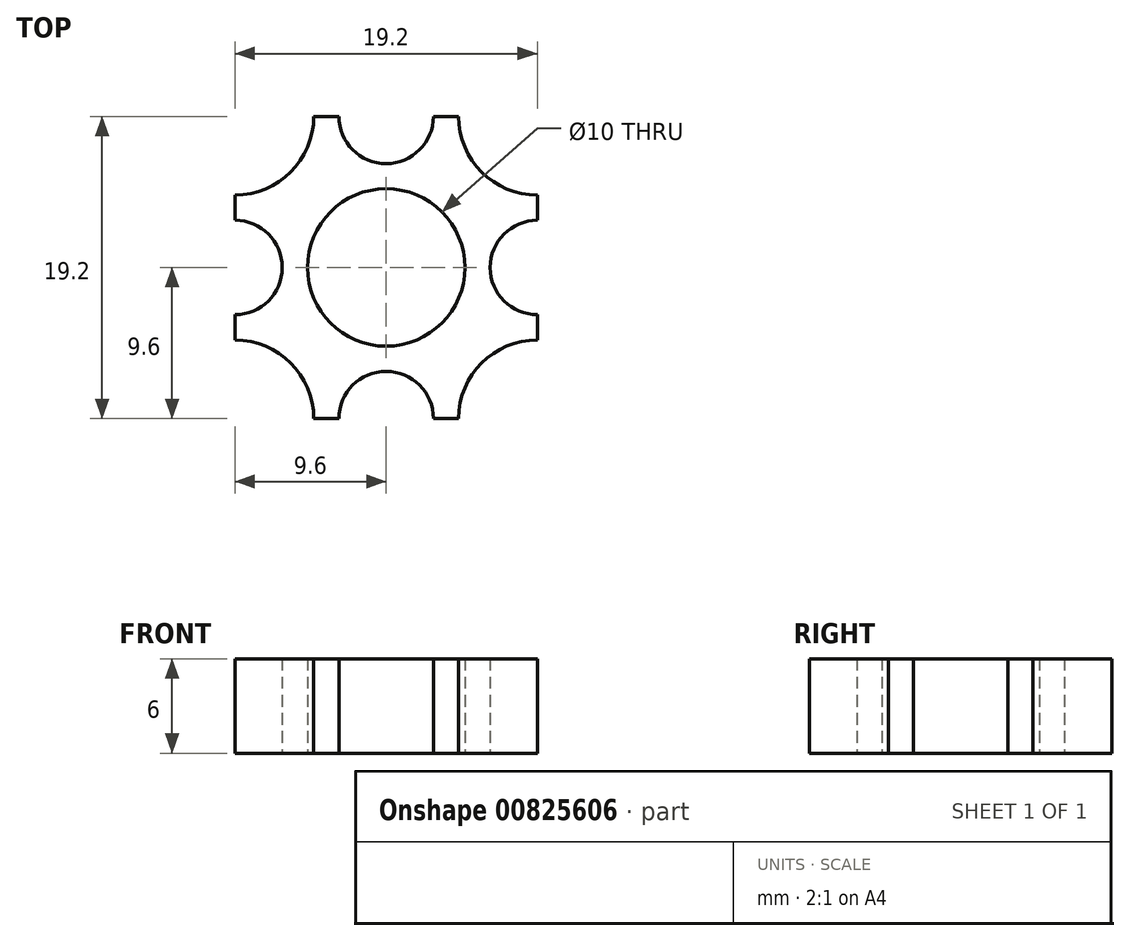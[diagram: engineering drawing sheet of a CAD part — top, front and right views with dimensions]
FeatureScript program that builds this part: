
annotation { "Feature Type Name" : "Feature", "Feature Type Description" : "" }
export const myFeature = defineFeature(function(context is Context, id is Id, definition is map)
    precondition{}
    {
        {
            var Q0;
            Q0=qCreatedBy(makeId("Top.planeOp"),FACE);
            var sketch = newSketch(context, id + "F0", { "sketchPlane" : qUnion([Q0])});
            skCircle(sketch, "E0", {"center": v(0, 0) * mm, "radius": 5 * mm});
            skCircle(sketch, "E1", {"center": v(-9.6, 0) * mm, "radius": 3 * mm});
            skCircle(sketch, "E2", {"center": v(-9.6, -9.6) * mm, "radius": 5 * mm});
            skCircle(sketch, "E3", {"center": v(0, -9.6) * mm, "radius": 3 * mm});
            skLineSegment(sketch, "E4.bottom", {"start": v(6.6, -45) * mm, "end": v(-45, -45) * mm});
            skLineSegment(sketch, "E4.top", {"start": v(6.6, 6.6) * mm, "end": v(-45, 6.6) * mm});
            skLineSegment(sketch, "E4.left", {"start": v(6.6, -45) * mm, "end": v(6.6, 6.6) * mm});
            skLineSegment(sketch, "E4.right", {"start": v(-45, -45) * mm, "end": v(-45, 6.6) * mm});
            skCircle(sketch, "E5.0.1.0", {"center": v(-9.6, 9.6) * mm, "radius": 5 * mm});
            skCircle(sketch, "E5.1.0.0", {"center": v(9.6, -9.6) * mm, "radius": 5 * mm});
            skCircle(sketch, "E5.1.1.0", {"center": v(9.6, 9.6) * mm, "radius": 5 * mm});
            skLineSegment(sketch, "E5.direction1", {"start": v(-9.6, -9.6) * mm, "end": v(9.6, -9.6) * mm, "construction": true});
            skLineSegment(sketch, "E5.direction2", {"start": v(-9.6, -9.6) * mm, "end": v(-9.6, 9.6) * mm, "construction": true});
            skCircle(sketch, "E6.0.1.0", {"center": v(-9.6, -19.2) * mm, "radius": 3 * mm});
            skCircle(sketch, "E6.0.1.1", {"center": v(0, -19.2) * mm, "radius": 5 * mm});
            skCircle(sketch, "E6.0.1.2", {"center": v(0, -28.8) * mm, "radius": 3 * mm});
            skCircle(sketch, "E6.0.1.3", {"center": v(-9.6, -28.8) * mm, "radius": 5 * mm});
            skCircle(sketch, "E6.0.2.0", {"center": v(-9.6, -38.4) * mm, "radius": 3 * mm});
            skCircle(sketch, "E6.0.2.1", {"center": v(0, -38.4) * mm, "radius": 5 * mm});
            skCircle(sketch, "E6.0.2.3", {"center": v(-9.6, -48) * mm, "radius": 5 * mm});
            skCircle(sketch, "E6.1.0.0", {"center": v(-28.8, 0) * mm, "radius": 3 * mm});
            skCircle(sketch, "E6.1.0.1", {"center": v(-19.2, 0) * mm, "radius": 5 * mm});
            skCircle(sketch, "E6.1.0.2", {"center": v(-19.2, -9.6) * mm, "radius": 3 * mm});
            skCircle(sketch, "E6.1.0.3", {"center": v(-28.8, -9.6) * mm, "radius": 5 * mm});
            skCircle(sketch, "E6.1.1.0", {"center": v(-28.8, -19.2) * mm, "radius": 3 * mm});
            skCircle(sketch, "E6.1.1.1", {"center": v(-19.2, -19.2) * mm, "radius": 5 * mm});
            skCircle(sketch, "E6.1.1.2", {"center": v(-19.2, -28.8) * mm, "radius": 3 * mm});
            skCircle(sketch, "E6.1.1.3", {"center": v(-28.8, -28.8) * mm, "radius": 5 * mm});
            skCircle(sketch, "E6.1.2.0", {"center": v(-28.8, -38.4) * mm, "radius": 3 * mm});
            skCircle(sketch, "E6.1.2.1", {"center": v(-19.2, -38.4) * mm, "radius": 5 * mm});
            skCircle(sketch, "E6.1.2.3", {"center": v(-28.8, -48) * mm, "radius": 5 * mm});
            skCircle(sketch, "E6.2.0.1", {"center": v(-38.4, 0) * mm, "radius": 5 * mm});
            skCircle(sketch, "E6.2.0.2", {"center": v(-38.4, -9.6) * mm, "radius": 3 * mm});
            skCircle(sketch, "E6.2.0.3", {"center": v(-48, -9.6) * mm, "radius": 5 * mm});
            skCircle(sketch, "E6.2.1.1", {"center": v(-38.4, -19.2) * mm, "radius": 5 * mm});
            skCircle(sketch, "E6.2.1.2", {"center": v(-38.4, -28.8) * mm, "radius": 3 * mm});
            skCircle(sketch, "E6.2.1.3", {"center": v(-48, -28.8) * mm, "radius": 5 * mm});
            skCircle(sketch, "E6.2.2.1", {"center": v(-38.4, -38.4) * mm, "radius": 5 * mm});
            skCircle(sketch, "E6.2.2.3", {"center": v(-48, -48) * mm, "radius": 5 * mm});
            skLineSegment(sketch, "E6.direction1", {"start": v(-9.6, -9.6) * mm, "end": v(-28.8, -9.6) * mm, "construction": true});
            skLineSegment(sketch, "E6.direction2", {"start": v(-9.6, -9.6) * mm, "end": v(-9.6, -28.8) * mm, "construction": true});
            skCircle(sketch, "E7.0.2.0", {"center": v(9.6, -28.8) * mm, "radius": 5 * mm});
            skCircle(sketch, "E7.0.3.0", {"center": v(9.6, -48) * mm, "radius": 5 * mm});
            skCircle(sketch, "E7.2.0.0", {"center": v(-28.8, 9.6) * mm, "radius": 5 * mm});
            skCircle(sketch, "E7.3.0.0", {"center": v(-48, 9.6) * mm, "radius": 5 * mm});
            skLineSegment(sketch, "E7.direction1", {"start": v(9.6, 9.6) * mm, "end": v(-9.6, 9.6) * mm, "construction": true});
            skLineSegment(sketch, "E7.direction2", {"start": v(9.6, 9.6) * mm, "end": v(9.6, -9.6) * mm, "construction": true});
            skSolve(sketch);
        }
        {
            var Q0;
            Q0=makeQuery(id+"F0.imprint","IMPRINT",FACE,{"disambiguationData":[TD([[makeQuery(id+"F0.imprint","IMPRINT",EDGE,{"derivedFrom":sQuery(id+"F0.wireOp",EDGE,"E0")}),-1.0]])]});
            extrude(context, id + "F1", {"entities" : qUnion([Q0]), "depth" : 6 * mm, "offsetDistance" : 25 * mm});
        }
        {
            var Q0;
            Q0=qCreatedBy(makeId("Top.planeOp"),FACE);
            var sketch = newSketch(context, id + "F2", { "sketchPlane" : qUnion([Q0])});
            skLineSegment(sketch, "E8.bottom", {"start": v(-28.8, -9.6) * mm, "end": v(-9.6, -9.6) * mm});
            skLineSegment(sketch, "E8.top", {"start": v(-28.8, -28.8) * mm, "end": v(-9.6, -28.8) * mm});
            skLineSegment(sketch, "E8.left", {"start": v(-28.8, -9.6) * mm, "end": v(-28.8, -28.8) * mm});
            skLineSegment(sketch, "E8.right", {"start": v(-9.6, -9.6) * mm, "end": v(-9.6, -28.8) * mm});
            skSolve(sketch);
        }
        {
            var Q0;
            Q0=makeQuery(id+"F2.imprint","IMPRINT",FACE,{"disambiguationData":[TD([[makeQuery(id+"F2.imprint","IMPRINT",EDGE,{"derivedFrom":sQuery(id+"F2.wireOp",EDGE,"E8.bottom")}),-1.0]])]});
            extrude(context, id + "F3", {"entities" : qUnion([Q0]), "operationType" : NewBodyOperationType.INTERSECT, "depth" : 6 * mm, "offsetDistance" : 25 * mm});
        }
    });
